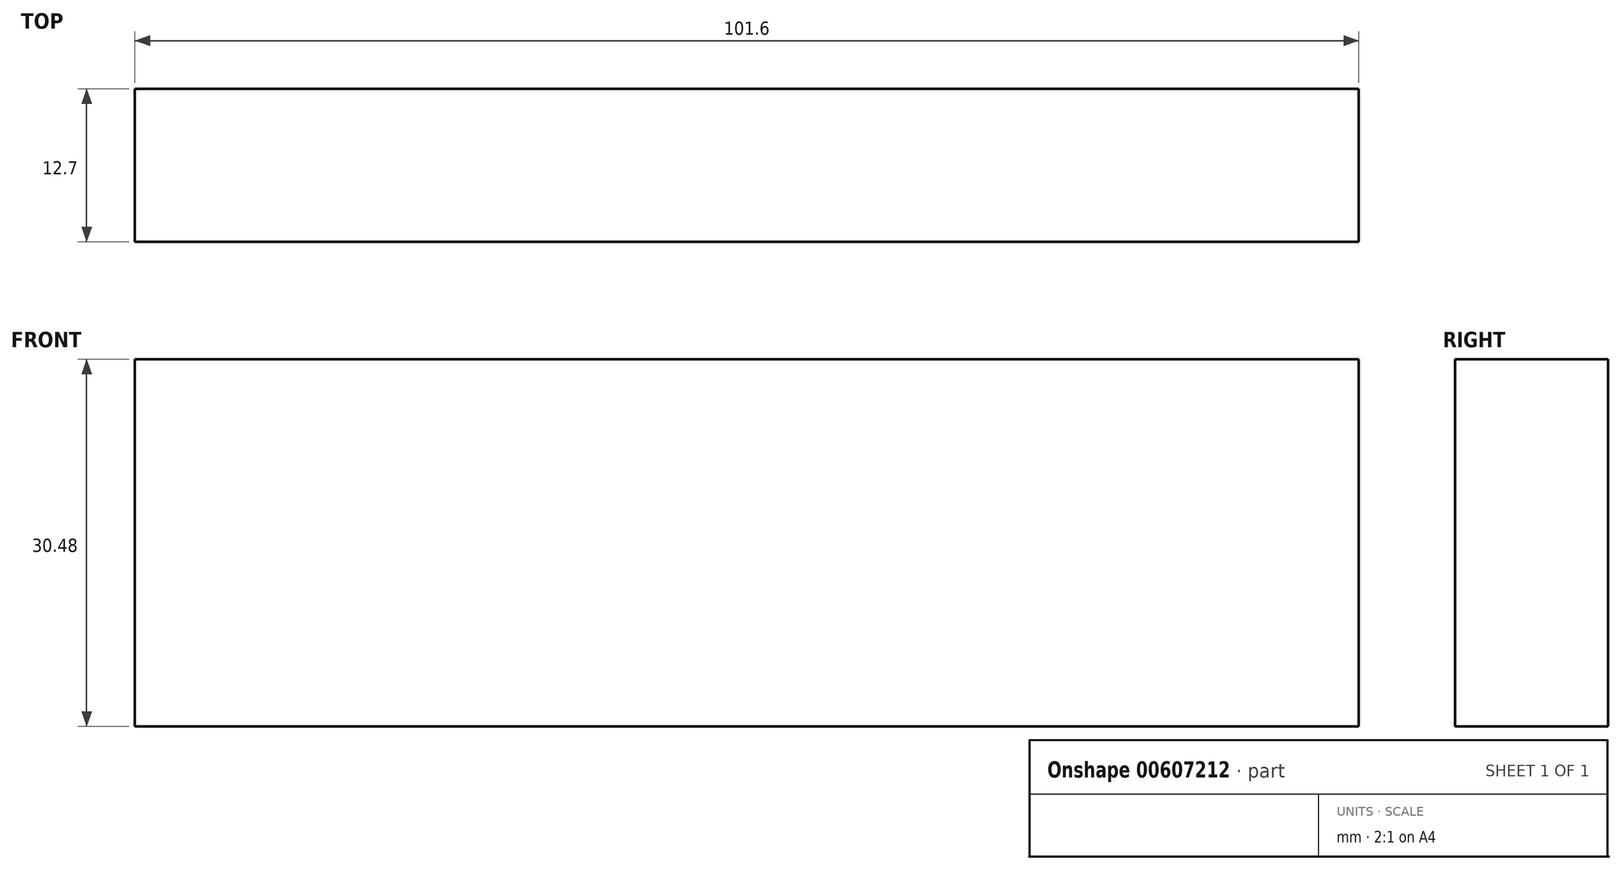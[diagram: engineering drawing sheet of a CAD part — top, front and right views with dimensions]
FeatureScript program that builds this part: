
annotation { "Feature Type Name" : "Feature", "Feature Type Description" : "" }
export const myFeature = defineFeature(function(context is Context, id is Id, definition is map)
    precondition{}
    {
        {
            var Q0;
            Q0=qCreatedBy(makeId("Front.planeOp"),FACE);
            var sketch = newSketch(context, id + "F0", { "sketchPlane" : qUnion([Q0])});
            skLineSegment(sketch, "E0.bottom", {"start": v(-48.13, 17.56) * mm, "end": v(53.47, 17.56) * mm});
            skLineSegment(sketch, "E0.top", {"start": v(-48.13, -12.92) * mm, "end": v(53.47, -12.92) * mm});
            skLineSegment(sketch, "E0.left", {"start": v(-48.13, 17.56) * mm, "end": v(-48.13, -12.92) * mm});
            skLineSegment(sketch, "E0.right", {"start": v(53.47, 17.56) * mm, "end": v(53.47, -12.92) * mm});
            skSolve(sketch);
        }
        {
            var Q0;
            Q0=makeQuery(id+"F0.imprint","IMPRINT",FACE,{"disambiguationData":[TD([[makeQuery(id+"F0.imprint","IMPRINT",EDGE,{"derivedFrom":sQuery(id+"F0.wireOp",EDGE,"E0.bottom")}),-1.0]])]});
            extrude(context, id + "F1", {"entities" : qUnion([Q0]), "depth" : 12.7 * mm, "offsetDistance" : 25.4 * mm});
        }
    });
